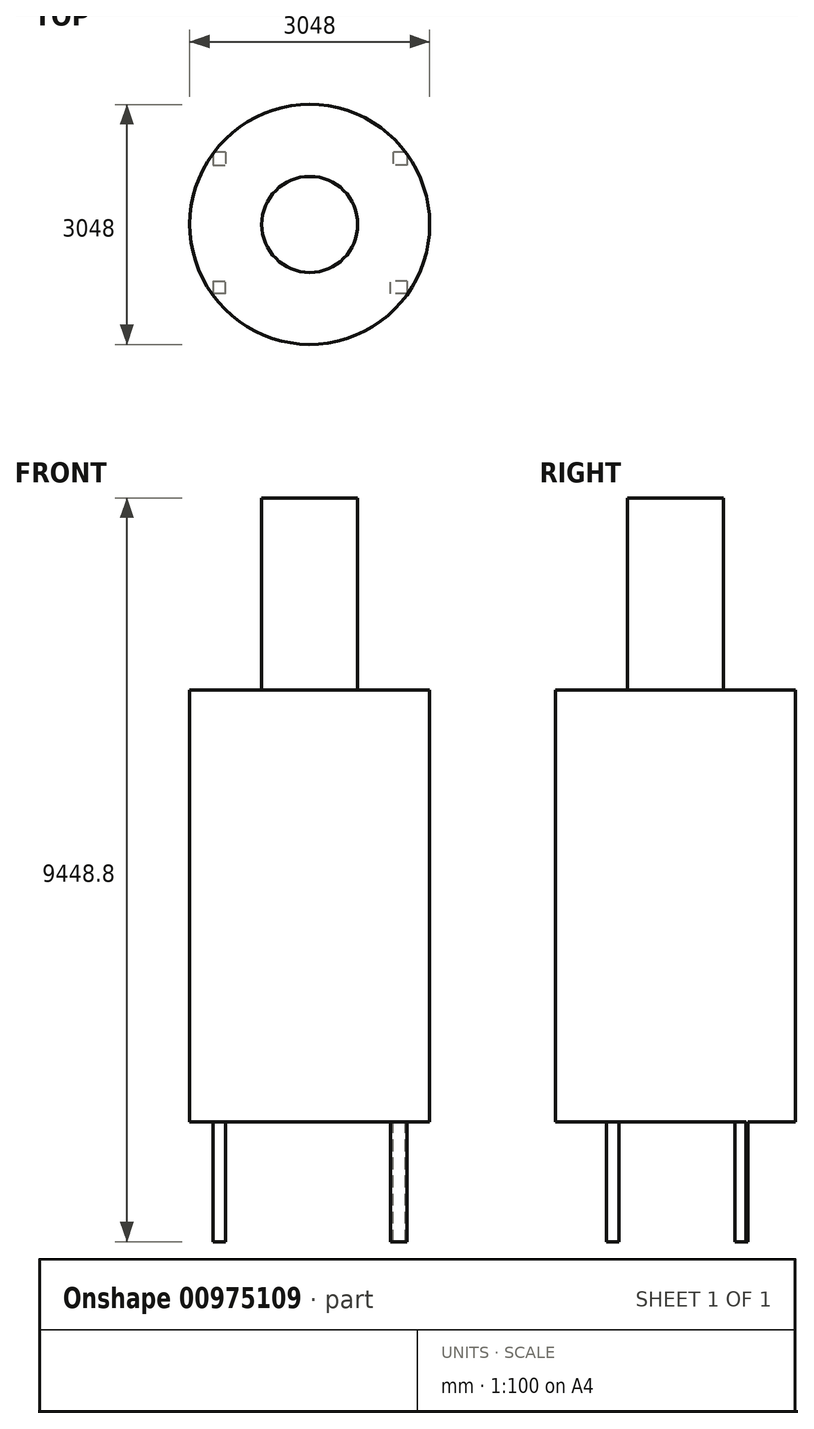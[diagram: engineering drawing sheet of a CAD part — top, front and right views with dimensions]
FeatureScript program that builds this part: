
annotation { "Feature Type Name" : "Feature", "Feature Type Description" : "" }
export const myFeature = defineFeature(function(context is Context, id is Id, definition is map)
    precondition{}
    {
        {
            var Q0;
            Q0=qCreatedBy(makeId("Top.planeOp"),FACE);
            var sketch = newSketch(context, id + "F0", { "sketchPlane" : qUnion([Q0])});
            skCircle(sketch, "E0", {"center": v(0, 0) * mm, "radius": 1524 * mm});
            skPoint(sketch, "E1", {"position": v(1225.8, 905.54) * mm});
            skSolve(sketch);
        }
        {
            var Q0;
            Q0=makeQuery(id+"F0.imprint","IMPRINT",FACE,{"disambiguationData":[TD([[makeQuery(id+"F0.imprint","IMPRINT",EDGE,{"derivedFrom":sQuery(id+"F0.wireOp",EDGE,"E0")}),1.0]])]});
            extrude(context, id + "F1", {"entities" : qUnion([Q0]), "depth" : 5486.4 * mm, "offsetDistance" : 25.4 * mm});
        }
        {
            var Q0;
            Q0=makeQuery(id+"F1.opExtrude","CAP_FACE",FACE,{"disambiguationData":[OSD([sQuery(id+"F0.wireOp",EDGE,"E0")])],"isStart":false});
            var sketch = newSketch(context, id + "F2", { "sketchPlane" : qUnion([Q0])});
            skCircle(sketch, "E2", {"center": v(0, 0) * mm, "radius": 609.6 * mm});
            skPoint(sketch, "E3", {"position": v(609.6, 0) * mm});
            skSolve(sketch);
        }
        {
            var Q0;
            Q0=makeQuery(id+"F2.imprint","IMPRINT",FACE,{"disambiguationData":[TD([[makeQuery(id+"F2.imprint","IMPRINT",EDGE,{"derivedFrom":sQuery(id+"F2.wireOp",EDGE,"E2")}),1.0]])]});
            extrude(context, id + "F3", {"entities" : qUnion([Q0]), "operationType" : NewBodyOperationType.ADD, "depth" : 2438.4 * mm, "offsetDistance" : 25.4 * mm});
        }
        {
            var Q0;
            Q0=makeQuery(id+"F0.imprint","IMPRINT",FACE,{"disambiguationData":[TD([[makeQuery(id+"F0.imprint","IMPRINT",EDGE,{"derivedFrom":sQuery(id+"F0.wireOp",EDGE,"E0")}),1.0]])]});
            var sketch = newSketch(context, id + "F4", { "sketchPlane" : qUnion([Q0])});
            skPoint(sketch, "E4", {"position": v(0, 0) * mm});
            skLineSegment(sketch, "E5.bottom", {"start": v(1236.47, 918.41) * mm, "end": v(-1228.84, 918.41) * mm});
            skLineSegment(sketch, "E5.top", {"start": v(1236.47, -881.88) * mm, "end": v(-1228.84, -881.88) * mm});
            skLineSegment(sketch, "E5.left", {"start": v(1236.47, 918.41) * mm, "end": v(1236.47, -881.88) * mm});
            skLineSegment(sketch, "E5.right", {"start": v(-1228.84, 918.41) * mm, "end": v(-1228.84, -881.88) * mm});
            skLineSegment(sketch, "E6.bottom", {"start": v(1236.47, 918.41) * mm, "end": v(1060.04, 918.41) * mm});
            skLineSegment(sketch, "E6.top", {"start": v(1236.47, 754.51) * mm, "end": v(1060.04, 754.51) * mm});
            skLineSegment(sketch, "E6.left", {"start": v(1236.47, 918.41) * mm, "end": v(1236.47, 754.51) * mm});
            skLineSegment(sketch, "E6.right", {"start": v(1060.04, 918.41) * mm, "end": v(1060.04, 754.51) * mm});
            skLineSegment(sketch, "E7.bottom", {"start": v(1236.47, -881.88) * mm, "end": v(1022.4, -881.88) * mm});
            skLineSegment(sketch, "E7.top", {"start": v(1236.47, -721.85) * mm, "end": v(1022.4, -721.85) * mm});
            skLineSegment(sketch, "E7.left", {"start": v(1236.47, -881.88) * mm, "end": v(1236.47, -721.85) * mm});
            skLineSegment(sketch, "E7.right", {"start": v(1022.4, -881.88) * mm, "end": v(1022.4, -721.85) * mm});
            skLineSegment(sketch, "E8.bottom", {"start": v(-1228.84, 918.41) * mm, "end": v(-1069.02, 918.41) * mm});
            skLineSegment(sketch, "E8.top", {"start": v(-1228.84, 754.51) * mm, "end": v(-1069.02, 754.51) * mm});
            skLineSegment(sketch, "E8.left", {"start": v(-1228.84, 918.41) * mm, "end": v(-1228.84, 754.51) * mm});
            skLineSegment(sketch, "E8.right", {"start": v(-1069.02, 918.41) * mm, "end": v(-1069.02, 754.51) * mm});
            skLineSegment(sketch, "E9.bottom", {"start": v(-1228.84, -881.88) * mm, "end": v(-1069.02, -881.88) * mm});
            skLineSegment(sketch, "E9.top", {"start": v(-1228.84, -721.85) * mm, "end": v(-1069.02, -721.85) * mm});
            skLineSegment(sketch, "E9.left", {"start": v(-1228.84, -881.88) * mm, "end": v(-1228.84, -721.85) * mm});
            skLineSegment(sketch, "E9.right", {"start": v(-1069.02, -881.88) * mm, "end": v(-1069.02, -721.85) * mm});
            skSolve(sketch);
        }
        {
            var Q0;
            {var subQ4=sQuery(id+"F4.wireOp",EDGE,"E9.top");Q0=makeQuery(id+"F4.imprint","IMPRINT",FACE,{"disambiguationData":[TD([[makeQuery(id+"F4.imprint","IMPRINT",EDGE,{"derivedFrom":subQ4}),-1.0]])]});}
            var Q1;
            {var subQ1=sQuery(id+"F4.wireOp",EDGE,"E8.top");Q1=makeQuery(id+"F4.imprint","IMPRINT",FACE,{"disambiguationData":[TD([[makeQuery(id+"F4.imprint","IMPRINT",EDGE,{"derivedFrom":subQ1}),1.0]])]});}
            var Q2;
            {var subQ1=sQuery(id+"F4.wireOp",EDGE,"E6.top");Q2=makeQuery(id+"F4.imprint","IMPRINT",FACE,{"disambiguationData":[TD([[makeQuery(id+"F4.imprint","IMPRINT",EDGE,{"derivedFrom":subQ1}),-1.0]])]});}
            var Q3;
            {var subQ4=sQuery(id+"F4.wireOp",EDGE,"E7.top");Q3=makeQuery(id+"F4.imprint","IMPRINT",FACE,{"disambiguationData":[TD([[makeQuery(id+"F4.imprint","IMPRINT",EDGE,{"derivedFrom":subQ4}),1.0]])]});}
            extrude(context, id + "F5", {"entities" : qUnion([Q0, Q1, Q2, Q3]), "operationType" : NewBodyOperationType.ADD, "oppositeDirection" : true, "depth" : 1524 * mm, "offsetDistance" : 25.4 * mm});
        }
    });
